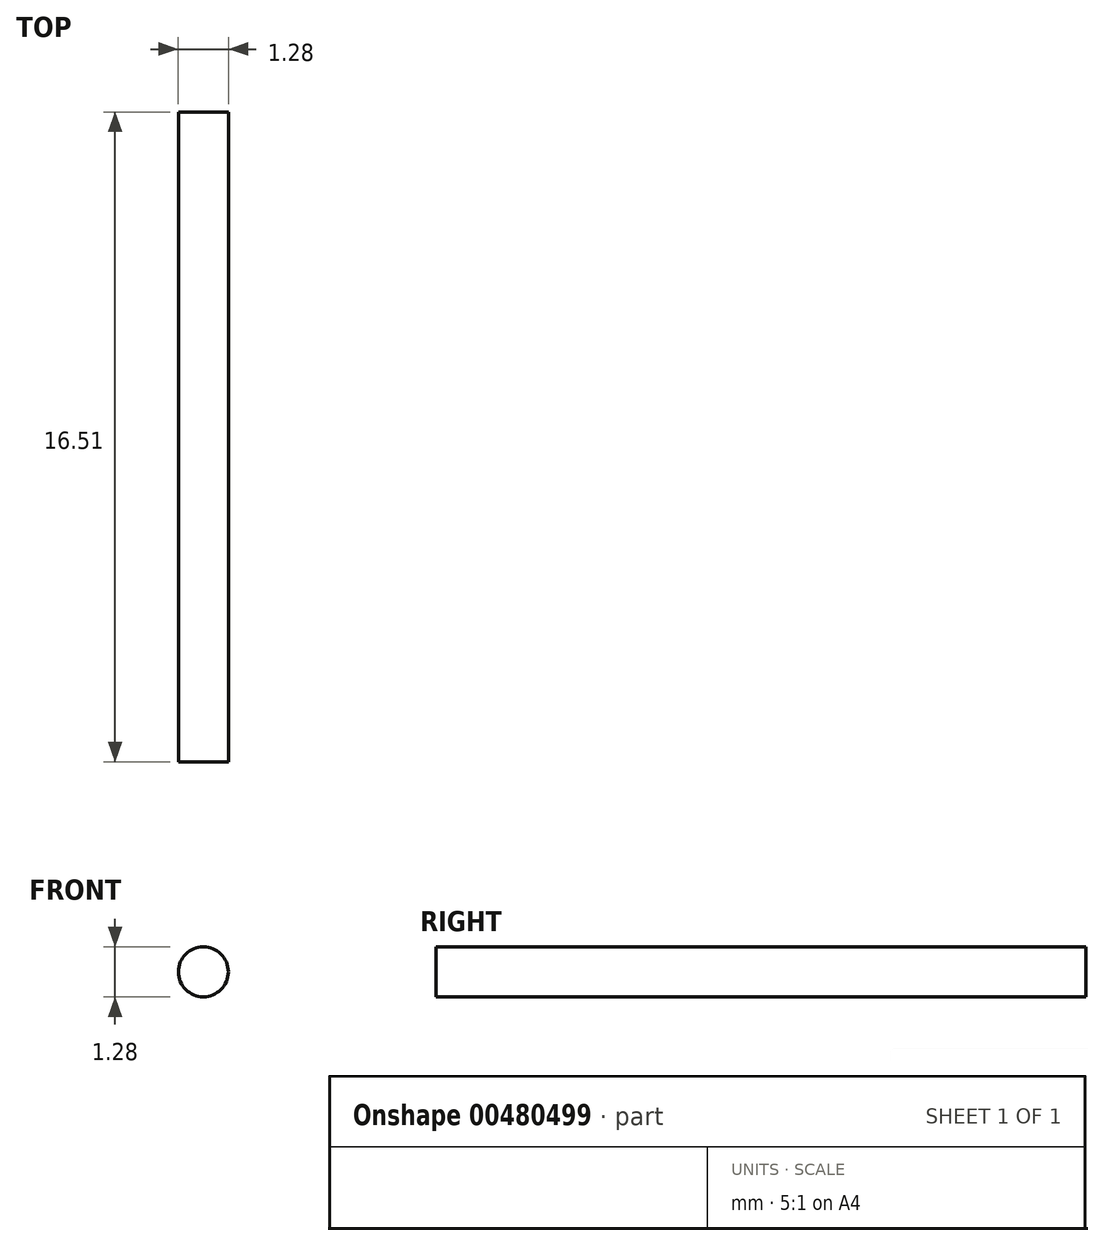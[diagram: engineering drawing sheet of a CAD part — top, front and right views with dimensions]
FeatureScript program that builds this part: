
annotation { "Feature Type Name" : "Feature", "Feature Type Description" : "" }
export const myFeature = defineFeature(function(context is Context, id is Id, definition is map)
    precondition{}
    {
        {
            var Q0;
            Q0=qCreatedBy(makeId("Front.planeOp"),FACE);
            var sketch = newSketch(context, id + "F0", { "sketchPlane" : qUnion([Q0])});
            skCircle(sketch, "E0", {"center": v(0, 0) * mm, "radius": 0.64 * mm});
            skSolve(sketch);
        }
        {
            var Q0;
            Q0 = qSketchRegion(id + "F0", true);
            extrude(context, id + "F1", {"entities" : qUnion([Q0]), "depth" : 16.5 * mm});
        }
    });
